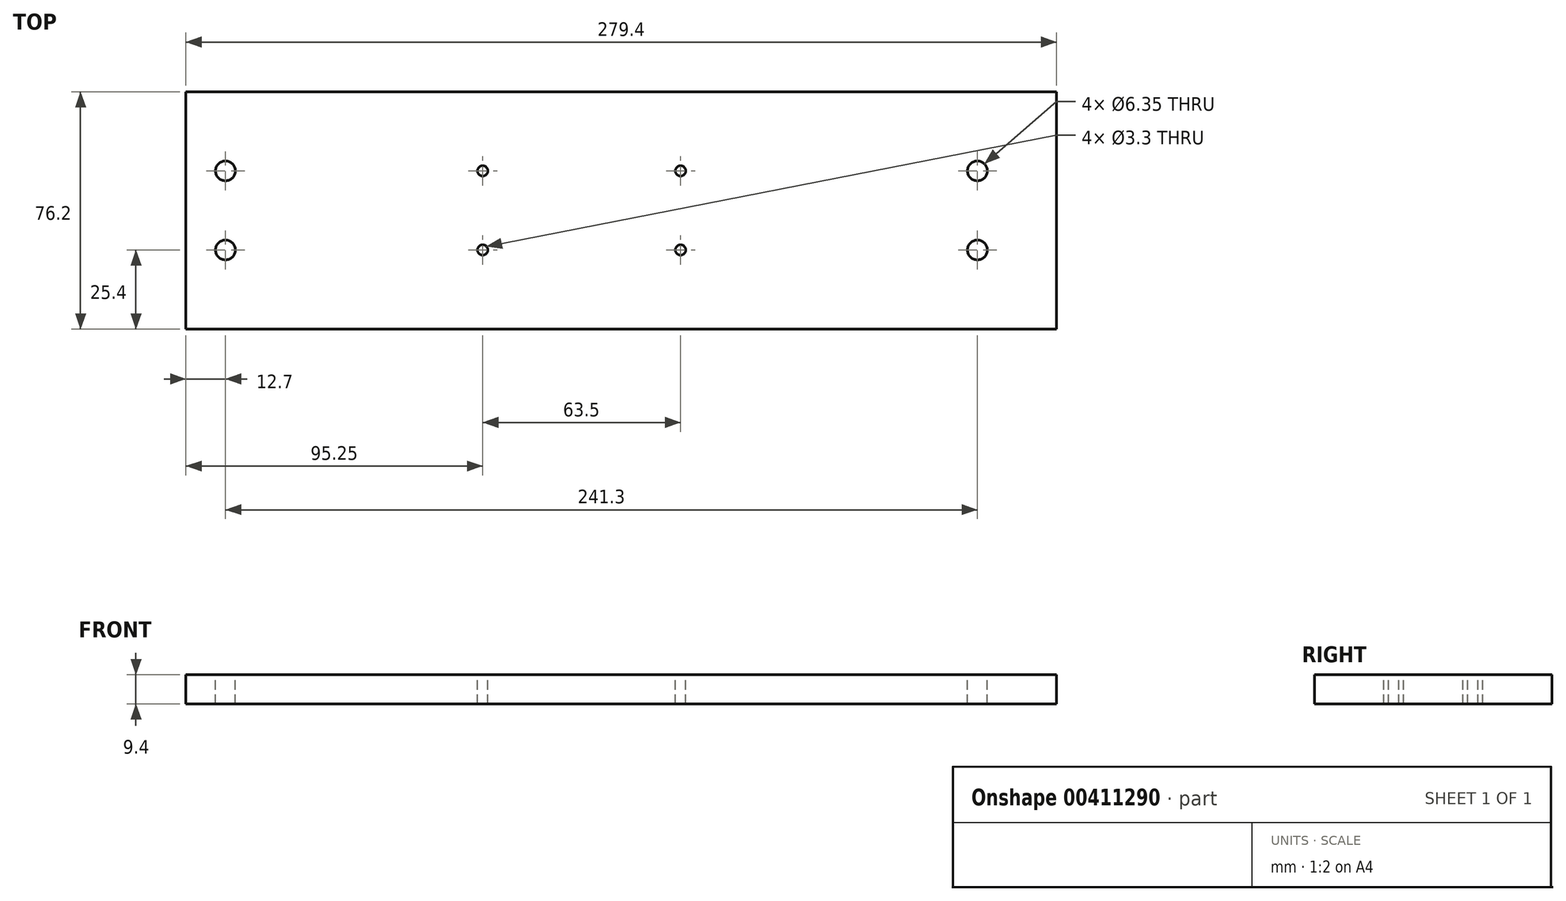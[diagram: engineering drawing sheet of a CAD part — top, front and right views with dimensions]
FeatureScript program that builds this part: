
annotation { "Feature Type Name" : "Feature", "Feature Type Description" : "" }
export const myFeature = defineFeature(function(context is Context, id is Id, definition is map)
    precondition{}
    {
        {
            var Q0;
            Q0=qCreatedBy(makeId("Top.planeOp"),FACE);
            var sketch = newSketch(context, id + "F0", { "sketchPlane" : qUnion([Q0])});
            skLineSegment(sketch, "E0.bottom", {"start": v(-139.7, 38.1) * mm, "end": v(139.7, 38.1) * mm});
            skLineSegment(sketch, "E0.top", {"start": v(-139.7, -38.1) * mm, "end": v(139.7, -38.1) * mm});
            skLineSegment(sketch, "E0.left", {"start": v(-139.7, 38.1) * mm, "end": v(-139.7, -38.1) * mm});
            skLineSegment(sketch, "E0.right", {"start": v(139.7, 38.1) * mm, "end": v(139.7, -38.1) * mm});
            skSolve(sketch);
        }
        {
            var Q0;
            Q0 = qSketchRegion(id + "F0", true);
            extrude(context, id + "F1", {"entities" : qUnion([Q0]), "depth" : 9.4 * mm});
        }
        {
            var Q0;
            Q0=makeQuery(id+"F1.opExtrude","CAP_FACE",FACE,{"disambiguationData":[OSD([sQuery(id+"F0.wireOp",EDGE,"E0.bottom"),sQuery(id+"F0.wireOp",EDGE,"E0.top"),sQuery(id+"F0.wireOp",EDGE,"E0.left"),sQuery(id+"F0.wireOp",EDGE,"E0.right")])],"isStart":false});
            var sketch = newSketch(context, id + "F2", { "sketchPlane" : qUnion([Q0])});
            skCircle(sketch, "E1", {"center": v(-127, 12.7) * mm, "radius": 3.18 * mm});
            skCircle(sketch, "E2", {"center": v(-127, -12.7) * mm, "radius": 3.18 * mm});
            skCircle(sketch, "E3", {"center": v(114.3, 12.7) * mm, "radius": 3.18 * mm});
            skCircle(sketch, "E4", {"center": v(114.3, -12.7) * mm, "radius": 3.18 * mm});
            skCircle(sketch, "E5", {"center": v(-44.45, 12.7) * mm, "radius": 1.65 * mm});
            skCircle(sketch, "E6", {"center": v(-44.45, -12.7) * mm, "radius": 1.65 * mm});
            skCircle(sketch, "E7", {"center": v(19.05, 12.7) * mm, "radius": 1.65 * mm});
            skCircle(sketch, "E8", {"center": v(19.05, -12.7) * mm, "radius": 1.65 * mm});
            skSolve(sketch);
        }
        {
            var Q0;
            Q0=makeQuery(id+"F2.imprint","IMPRINT",FACE,{"disambiguationData":[TD([[makeQuery(id+"F2.imprint","IMPRINT",EDGE,{"derivedFrom":sQuery(id+"F2.wireOp",EDGE,"E1")}),-1.0]])]});
            var Q1;
            Q1=sQuery(id+"F2.wireOp",EDGE,"E1");
            var Q2;
            Q2=sQuery(id+"F2.wireOp",EDGE,"E2");
            var Q3;
            Q3=sQuery(id+"F2.wireOp",EDGE,"E5");
            var Q4;
            Q4=sQuery(id+"F2.wireOp",EDGE,"E6");
            var Q5;
            Q5=sQuery(id+"F2.wireOp",EDGE,"E8");
            var Q6;
            Q6=sQuery(id+"F2.wireOp",EDGE,"E7");
            var Q7;
            Q7=sQuery(id+"F2.wireOp",EDGE,"E3");
            var Q8;
            Q8=sQuery(id+"F2.wireOp",EDGE,"E4");
            extrude(context, id + "F3", {"entities" : qUnion([Q0]), "operationType" : NewBodyOperationType.INTERSECT, "surfaceEntities" : qUnion([Q1, Q2, Q3, Q4, Q5, Q6, Q7, Q8]), "endBound" : BoundingType.SYMMETRIC, "oppositeDirection" : true, "depth" : 25.4 * mm});
        }
    });
